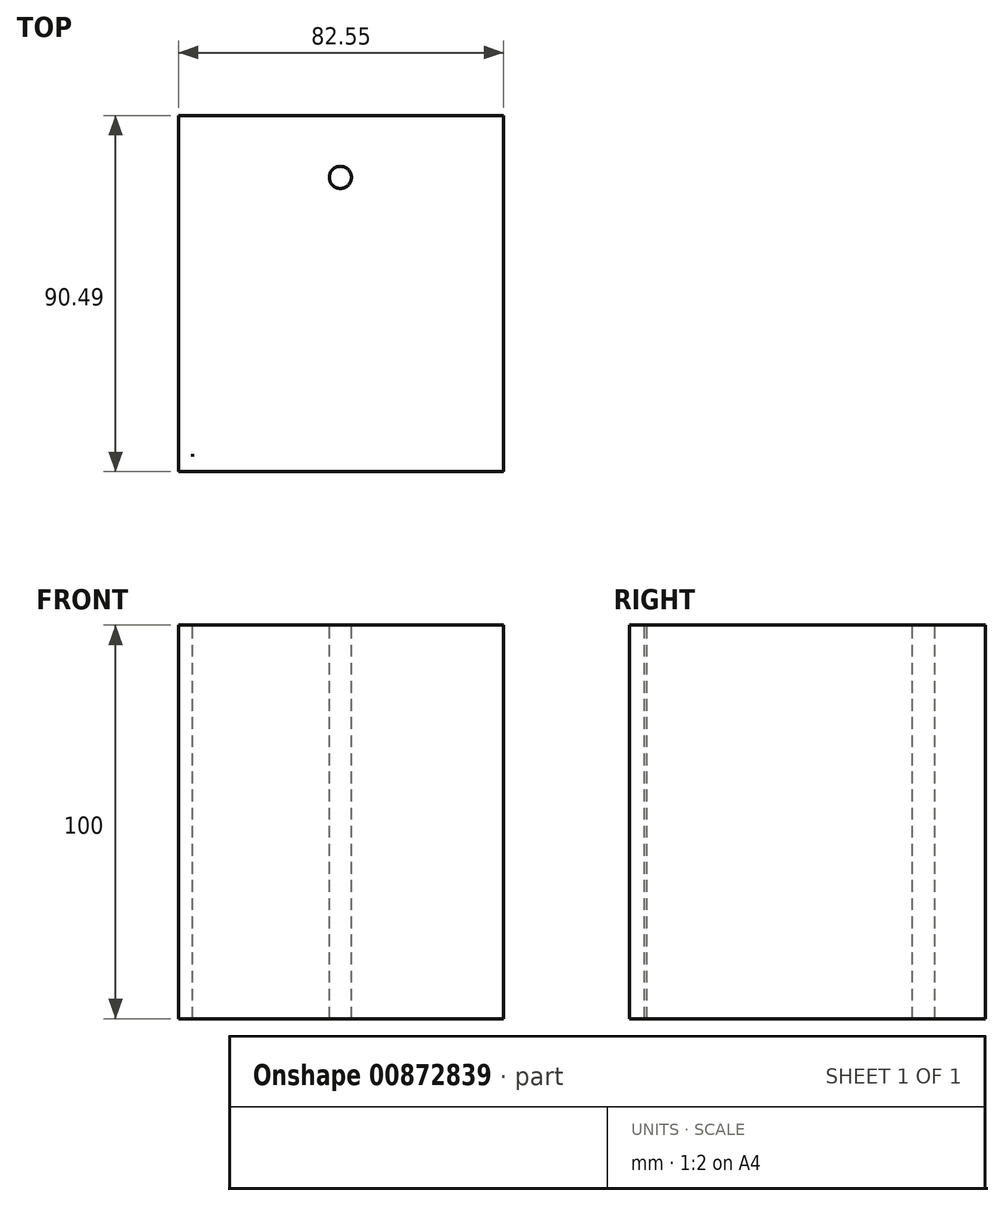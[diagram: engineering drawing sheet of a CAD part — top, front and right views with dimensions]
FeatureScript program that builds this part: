
annotation { "Feature Type Name" : "Feature", "Feature Type Description" : "" }
export const myFeature = defineFeature(function(context is Context, id is Id, definition is map)
    precondition{}
    {
        {
            var Q0;
            Q0=qCreatedBy(makeId("Top.planeOp"),FACE);
            var sketch = newSketch(context, id + "F0", { "sketchPlane" : qUnion([Q0])});
            skLineSegment(sketch, "E0", {"start": v(-41.12, 39.21) * mm, "end": v(41.43, 39.21) * mm});
            skLineSegment(sketch, "E1", {"start": v(41.43, 39.21) * mm, "end": v(41.43, -51.28) * mm});
            skLineSegment(sketch, "E2", {"start": v(41.43, -51.28) * mm, "end": v(-41.12, -51.28) * mm});
            skLineSegment(sketch, "E3", {"start": v(-41.12, -51.28) * mm, "end": v(-41.12, 39.21) * mm});
            skLineSegment(sketch, "E4", {"start": v(-37.5, 35.45) * mm, "end": v(-37.5, -46.83) * mm});
            skLineSegment(sketch, "E5", {"start": v(-37.5, 35.45) * mm, "end": v(37.83, 35.45) * mm});
            skLineSegment(sketch, "E6", {"start": v(37.83, 35.45) * mm, "end": v(37.65, -47.61) * mm});
            skLineSegment(sketch, "E7", {"start": v(37.65, -47.61) * mm, "end": v(-37.5, -47.46) * mm});
            skLineSegment(sketch, "E8", {"start": v(-37.5, -47.46) * mm, "end": v(-37.5, -46.83) * mm});
            skLineSegment(sketch, "E9", {"start": v(-37.5, 13.34) * mm, "end": v(37.78, 13.34) * mm});
            skCircle(sketch, "E10", {"center": v(0, 23.47) * mm, "radius": 2.8 * mm});
            skSolve(sketch);
        }
        {
            var Q0;
            Q0=sQuery(id+"F0.wireOp",EDGE,"E2");
            var Q1;
            Q1=sQuery(id+"F0.wireOp",EDGE,"E3");
            var Q2;
            Q2=sQuery(id+"F0.wireOp",EDGE,"E1");
            var Q3;
            Q3=sQuery(id+"F0.wireOp",EDGE,"E0");
            var Q4;
            Q4=sQuery(id+"F0.wireOp",EDGE,"E10");
            var Q5;
            Q5=sQuery(id+"F0.wireOp",EDGE,"E8");
            extrude(context, id + "F1", {"bodyType" : ToolBodyType.SURFACE, "surfaceEntities" : qUnion([Q0, Q1, Q2, Q3, Q4, Q5]), "depth" : 100 * mm, "offsetDistance" : 25.4 * mm});
        }
    });
